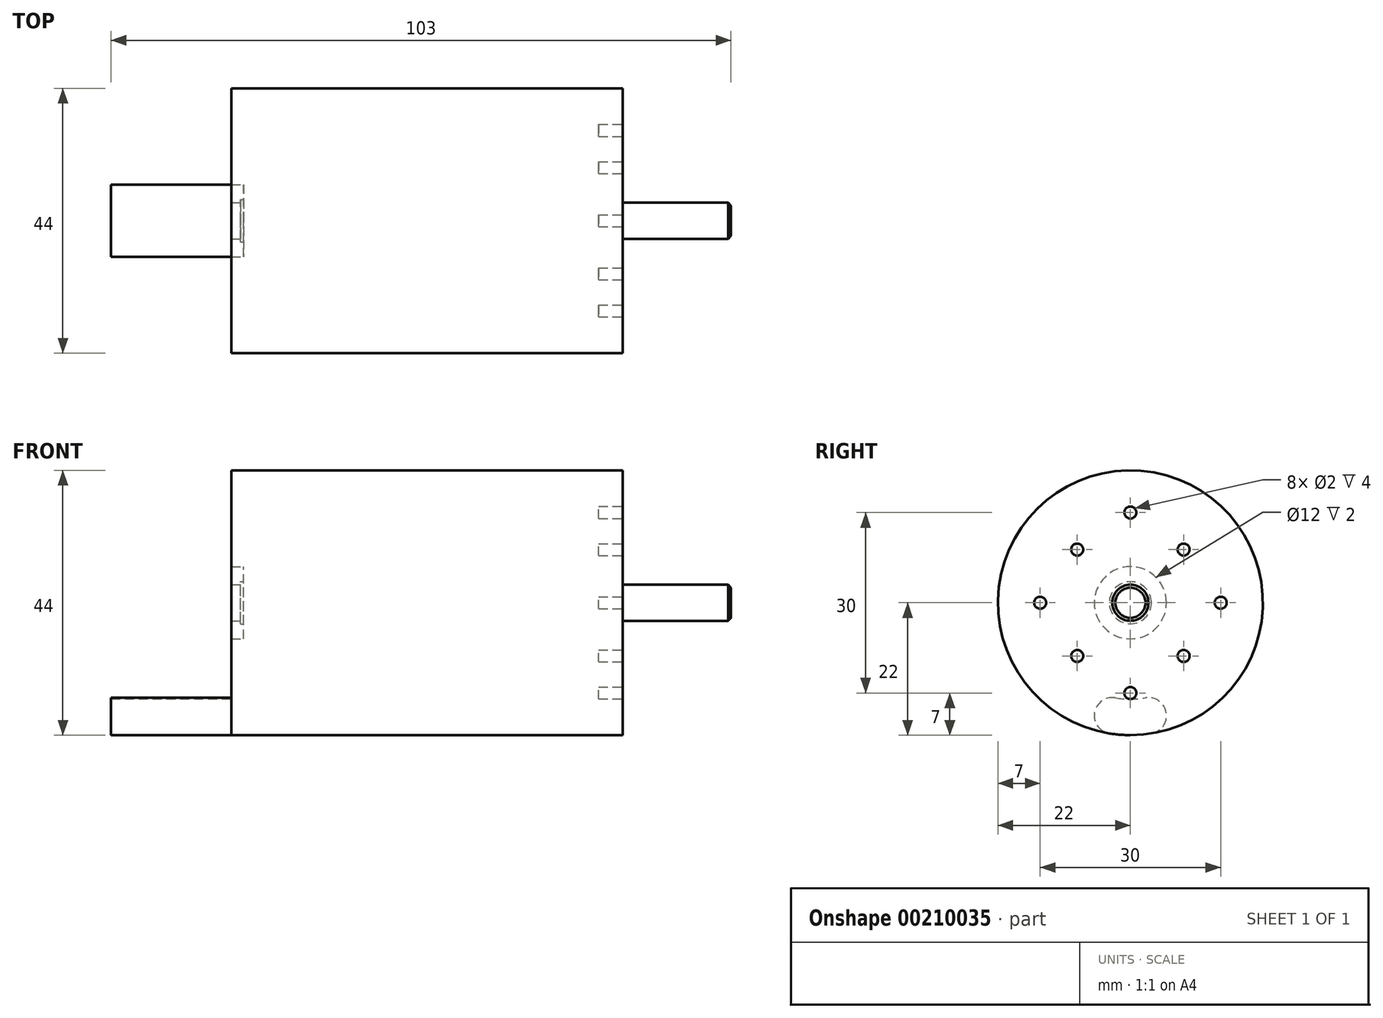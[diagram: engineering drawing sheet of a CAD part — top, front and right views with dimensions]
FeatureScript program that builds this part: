
annotation { "Feature Type Name" : "Feature", "Feature Type Description" : "" }
export const myFeature = defineFeature(function(context is Context, id is Id, definition is map)
    precondition{}
    {
        {
            var Q0;
            Q0=qCreatedBy(makeId("Right.planeOp"),FACE);
            var sketch = newSketch(context, id + "F0", { "sketchPlane" : qUnion([Q0])});
            skCircle(sketch, "E0", {"center": v(0, 0) * mm, "radius": 22 * mm});
            skSolve(sketch);
        }
        {
            var Q0;
            Q0 = qSketchRegion(id + "F0", true);
            extrude(context, id + "F1", {"entities" : qUnion([Q0]), "endBound" : BoundingType.SYMMETRIC, "depth" : 65 * mm});
        }
        {
            var Q0;
            Q0=makeQuery(id+"F1.opExtrude","CAP_FACE",FACE,{"disambiguationData":[OSD([sQuery(id+"F0.wireOp",EDGE,"E0")])],"isStart":false});
            var sketch = newSketch(context, id + "F2", { "sketchPlane" : qUnion([Q0])});
            skCircle(sketch, "E1", {"center": v(0, 0) * mm, "radius": 3 * mm});
            skSolve(sketch);
        }
        {
            var Q0;
            Q0 = qSketchRegion(id + "F2", true);
            extrude(context, id + "F3", {"entities" : qUnion([Q0]), "operationType" : NewBodyOperationType.ADD, "depth" : 18 * mm});
        }
        {
            var Q0;
            Q0=makeQuery(id+"F1.opExtrude","CAP_FACE",FACE,{"disambiguationData":[OSD([sQuery(id+"F0.wireOp",EDGE,"E0")])],"isStart":false});
            var sketch = newSketch(context, id + "F4", { "sketchPlane" : qUnion([Q0])});
            skCircle(sketch, "E2", {"center": v(0, 0) * mm, "radius": 15 * mm, "construction": true});
            skCircle(sketch, "E3", {"center": v(0, 15) * mm, "radius": 1 * mm});
            skCircle(sketch, "E4.1.0", {"center": v(-15, 0) * mm, "radius": 1 * mm});
            skCircle(sketch, "E4.2.0", {"center": v(0, -15) * mm, "radius": 1 * mm});
            skCircle(sketch, "E4.3.0", {"center": v(15, 0) * mm, "radius": 1 * mm});
            skCircle(sketch, "E5", {"center": v(0, 0) * mm, "radius": 12.5 * mm, "construction": true});
            skCircle(sketch, "E6", {"center": v(-8.84, 8.84) * mm, "radius": 1 * mm});
            skLineSegment(sketch, "E7", {"start": v(0, 0) * mm, "end": v(-13.52, 13.52) * mm, "construction": true});
            skLineSegment(sketch, "E8", {"start": v(0, 0) * mm, "end": v(0, 19.97) * mm, "construction": true});
            skCircle(sketch, "E9.1.0", {"center": v(-8.84, -8.84) * mm, "radius": 1 * mm});
            skCircle(sketch, "E9.2.0", {"center": v(8.84, -8.84) * mm, "radius": 1 * mm});
            skCircle(sketch, "E9.3.0", {"center": v(8.84, 8.84) * mm, "radius": 1 * mm});
            skSolve(sketch);
        }
        {
            var Q0;
            Q0 = qSketchRegion(id + "F4", true);
            extrude(context, id + "F5", {"entities" : qUnion([Q0]), "operationType" : NewBodyOperationType.REMOVE, "oppositeDirection" : true, "depth" : 4 * mm});
        }
        {
            var Q0;
            Q0=qCreatedBy(makeId("Front.planeOp"),FACE);
            var sketch = newSketch(context, id + "F6", { "sketchPlane" : qUnion([Q0])});
            skLineSegment(sketch, "E10", {"start": v(-32.5, 3) * mm, "end": v(-31, 3) * mm});
            skLineSegment(sketch, "E11", {"start": v(-31, 3) * mm, "end": v(-31, 3.5) * mm});
            skLineSegment(sketch, "E12", {"start": v(-31, 3.5) * mm, "end": v(-30.5, 3.5) * mm});
            skLineSegment(sketch, "E13", {"start": v(-30.5, 3.5) * mm, "end": v(-30.5, 6) * mm});
            skLineSegment(sketch, "E14", {"start": v(-30.5, 6) * mm, "end": v(-32.5, 6) * mm});
            skLineSegment(sketch, "E15", {"start": v(-32.5, 6) * mm, "end": v(-32.5, 3) * mm});
            skLineSegment(sketch, "E16", {"start": v(-49.5, 0) * mm, "end": v(65.27, 0) * mm, "construction": true});
            skSolve(sketch);
        }
        {
            var Q0;
            Q0 = qSketchRegion(id + "F6", true);
            var Q1;
            Q1=sQuery(id+"F6.wireOp",EDGE,"E16");
            revolve(context, id + "F7", {"operationType" : NewBodyOperationType.REMOVE, "entities" : qUnion([Q0]), "axis" : qUnion([Q1]), "revolveType" : RevolveType.FULL, "oppositeDirection" : true});
        }
        {
            var Q0;
            {var subQ0=sQuery(id+"F0.wireOp",EDGE,"E0");Q0=makeQuery(id+"F7.boolean.opBoolean","SPLIT",FACE,{"disambiguationData":[TD([makeQuery(id+"F1.opExtrude","SWEPT_FACE",FACE,{"disambiguationData":[OSD([subQ0])]})])],"derivedFrom":makeQuery(id+"F1.opExtrude","CAP_FACE",FACE,{"disambiguationData":[OSD([subQ0])],"isStart":true})});}
            var sketch = newSketch(context, id + "F8", { "sketchPlane" : qUnion([Q0])});
            skArc(sketch, "E17", {"start": v(3.47, -21.72) * mm, "mid": v(5.96, -18.29) * mm, "end": v(2.53, -15.8) * mm});
            skLineSegment(sketch, "E18", {"start": v(6, 14.15) * mm, "end": v(6, -25.56) * mm, "construction": true});
            skCircle(sketch, "E19", {"center": v(0, 0) * mm, "radius": 19 * mm, "construction": true});
            skArc(sketch, "E20", {"start": v(-2.53, -15.8) * mm, "mid": v(0, -16) * mm, "end": v(2.53, -15.8) * mm});
            skArc(sketch, "E21", {"start": v(-3.47, -21.72) * mm, "mid": v(0, -22) * mm, "end": v(3.47, -21.72) * mm});
            skArc(sketch, "E22.MirrorCS", {"start": v(-3.47, -21.72) * mm, "mid": v(-5.96, -18.29) * mm, "end": v(-2.53, -15.8) * mm});
            skSolve(sketch);
        }
        {
            var Q0;
            Q0 = qSketchRegion(id + "F8", true);
            extrude(context, id + "F9", {"entities" : qUnion([Q0]), "operationType" : NewBodyOperationType.ADD, "depth" : 20 * mm});
        }
        {
            var Q0;
            Q0=makeQuery(id+"F3.opExtrude","CAP_EDGE",EDGE,{"disambiguationData":[OSD([sQuery(id+"F2.wireOp",EDGE,"E1")])],"isStart":false});
            chamfer(context, id + "F10", {"entities" : qUnion([Q0]), "width" : .5 * mm, "tangentPropagation" : true});
        }
    });
